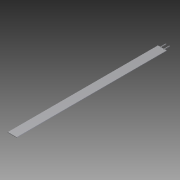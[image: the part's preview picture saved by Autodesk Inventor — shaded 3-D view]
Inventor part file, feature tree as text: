
AUTODESK INVENTOR PART (.ipt)
format: ipt  version: 2012 (Build 160160000, 160)  size: 135,168 bytes
history: native  units: in
note: dims shown in document units (in); Inventor stores cm internally (conversion verified against a paired STEP export)
features: reference x12, extrude x2, fillet x2, sketch x2
ambient origin geometry x8: Origin, YZ Plane, XZ Plane, XY Plane, X Axis, Y Axis, Z Axis, Center Point
bodies: Solid1 (feature_tree)
feature tree (18):
  extrude  "Extrusion1"  Depth=0.1181in
  extrude  "Extrusion2"  Depth=1.2175in TaperAngle=0.0deg
  fillet  "Fillet1"  Radius=0.2963in
  fillet  "Fillet2"  Radius=0.0354in
  sketch  "Sketch1"  dims[d0=3.1496in d1=0.1181in]
  reference  "Reference1"
  reference  "Reference2"
  reference  "Reference3"
  reference  "Reference4"
  reference  "Reference5"
  reference  "Reference6"
  reference  "Reference7"
  reference  "Reference8"
  sketch  "Sketch2"  dims[d2=33.4646in d3=0.0in d4=1.2175in d5=0.0in d6=0.2963in d7=0.0in d8=0.0354in d9=0.0354in]
  reference  "Reference9"
  reference  "Reference10"
  reference  "Reference11"
  reference  "Reference12"
